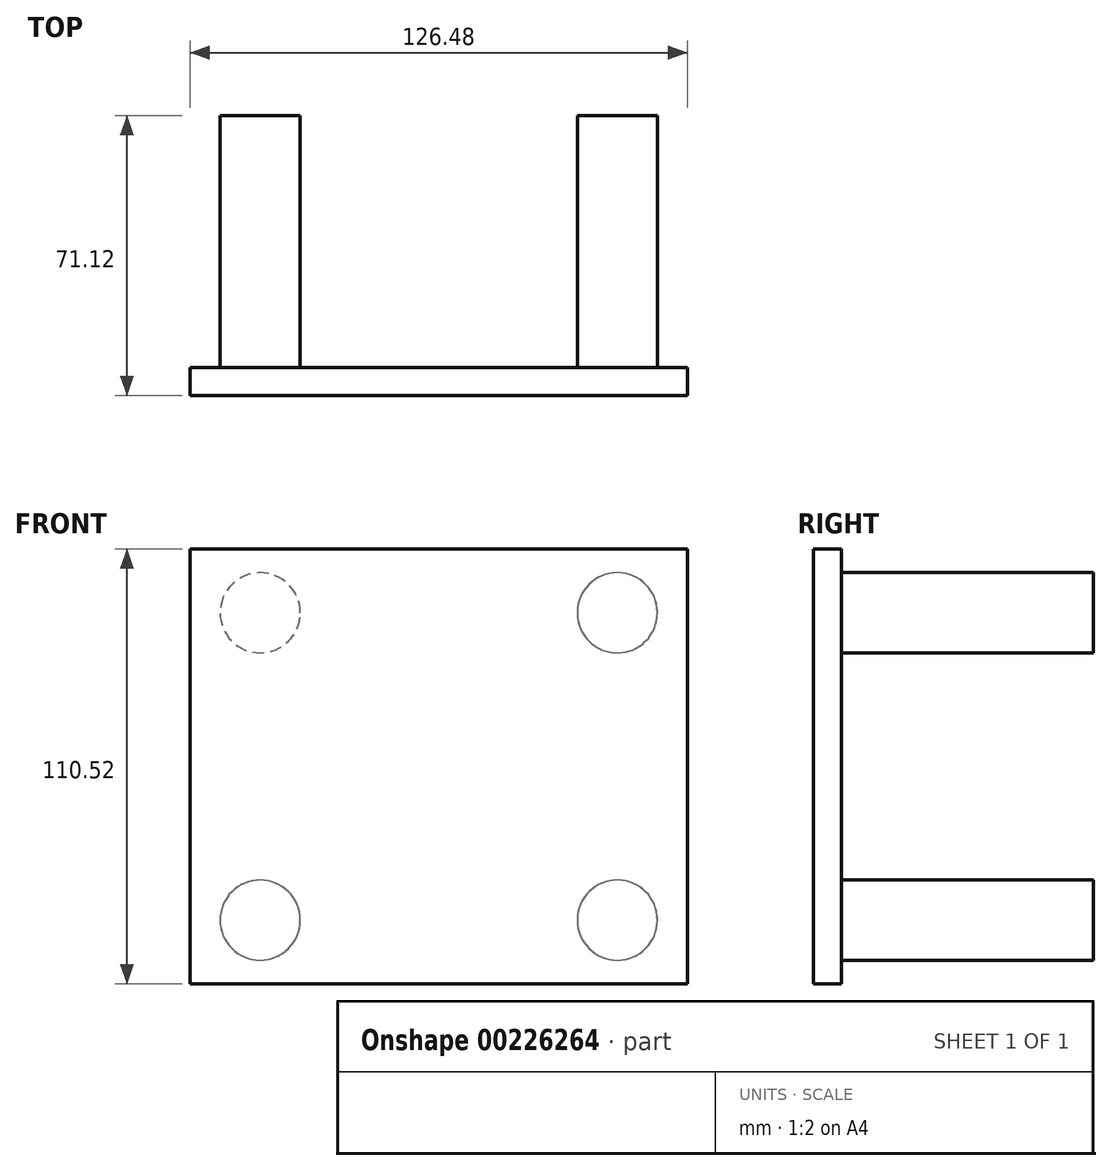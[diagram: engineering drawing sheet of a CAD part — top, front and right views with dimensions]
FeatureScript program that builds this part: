
annotation { "Feature Type Name" : "Feature", "Feature Type Description" : "" }
export const myFeature = defineFeature(function(context is Context, id is Id, definition is map)
    precondition{}
    {
        {
            var Q0;
            Q0=qCreatedBy(makeId("Front.planeOp"),FACE);
            var sketch = newSketch(context, id + "F0", { "sketchPlane" : qUnion([Q0])});
            skLineSegment(sketch, "E0.bottom", {"start": v(63.24, 55.26) * mm, "end": v(-63.24, 55.26) * mm});
            skLineSegment(sketch, "E0.top", {"start": v(63.24, -55.26) * mm, "end": v(-63.24, -55.26) * mm});
            skLineSegment(sketch, "E0.left", {"start": v(63.24, 55.26) * mm, "end": v(63.24, -55.26) * mm});
            skLineSegment(sketch, "E0.right", {"start": v(-63.24, 55.26) * mm, "end": v(-63.24, -55.26) * mm});
            skPoint(sketch, "E0.middle", {"position": v(0, 0) * mm});
            skSolve(sketch);
        }
        {
            var Q0;
            Q0=makeQuery(id+"F0.imprint","IMPRINT",FACE,{"disambiguationData":[TD([[makeQuery(id+"F0.imprint","IMPRINT",EDGE,{"derivedFrom":sQuery(id+"F0.wireOp",EDGE,"E0.bottom")}),1.0]])]});
            extrude(context, id + "F1", {"entities" : qUnion([Q0]), "depth" : 7.11 * mm});
        }
        {
            var Q0;
            Q0=makeQuery(id+"F1.opExtrude","CAP_FACE",FACE,{"disambiguationData":[OSD([sQuery(id+"F0.wireOp",EDGE,"E0.bottom"),sQuery(id+"F0.wireOp",EDGE,"E0.top"),sQuery(id+"F0.wireOp",EDGE,"E0.left"),sQuery(id+"F0.wireOp",EDGE,"E0.right")])],"isStart":true});
            var sketch = newSketch(context, id + "F2", { "sketchPlane" : qUnion([Q0])});
            skCircle(sketch, "E1", {"center": v(45.37, 39.04) * mm, "radius": 10.19 * mm});
            skCircle(sketch, "E2.MirrorC", {"center": v(45.37, -39.04) * mm, "radius": 10.19 * mm});
            skCircle(sketch, "E3.MirrorC", {"center": v(-45.37, -39.04) * mm, "radius": 10.19 * mm});
            skCircle(sketch, "E4.MirrorC", {"center": v(-45.37, 39.04) * mm, "radius": 10.19 * mm});
            skSolve(sketch);
        }
        {
            var Q0;
            Q0 = qSketchRegion(id + "F2", true);
            extrude(context, id + "F3", {"entities" : qUnion([Q0]), "operationType" : NewBodyOperationType.ADD, "depth" : 64 * mm});
        }
    });
